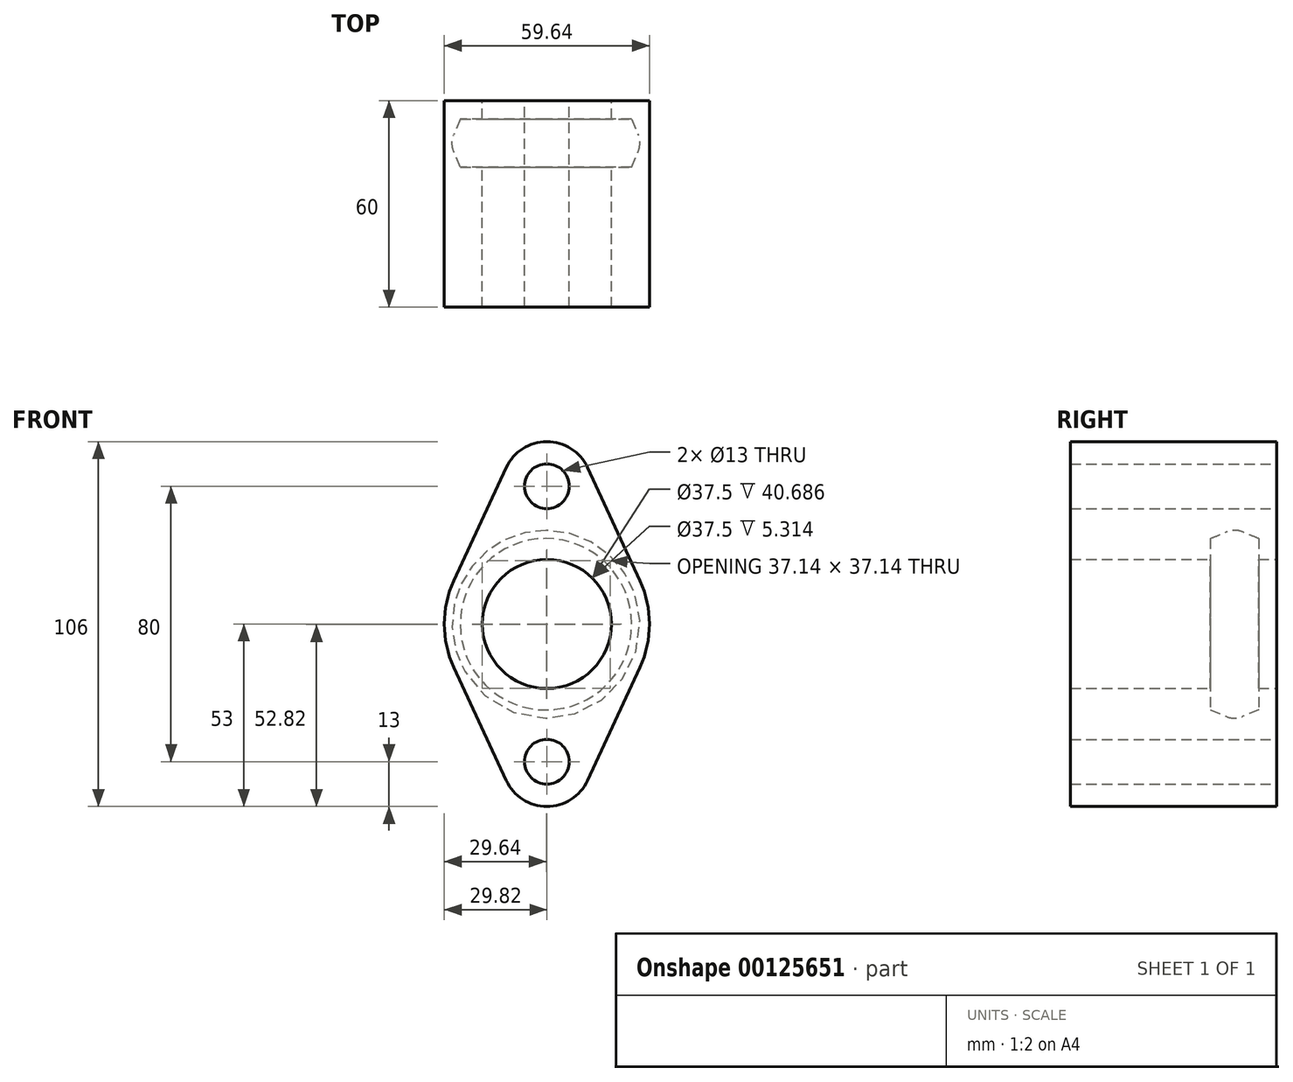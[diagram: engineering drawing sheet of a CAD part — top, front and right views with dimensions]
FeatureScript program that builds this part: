
annotation { "Feature Type Name" : "Feature", "Feature Type Description" : "" }
export const myFeature = defineFeature(function(context is Context, id is Id, definition is map)
    precondition{}
    {
        {
            var Q0;
            Q0=qCreatedBy(makeId("Front.planeOp"),FACE);
            var sketch = newSketch(context, id + "F0", { "sketchPlane" : qUnion([Q0])});
            skCircle(sketch, "E0", {"center": v(0, 0) * mm, "radius": 18.75 * mm});
            skCircle(sketch, "E1", {"center": v(0, 40) * mm, "radius": 6.5 * mm});
            skCircle(sketch, "E2", {"center": v(0, -40) * mm, "radius": 6.5 * mm});
            skArc(sketch, "E3", {"start": v(-27.05, 12.53) * mm, "mid": v(-29.82, 0) * mm, "end": v(-27.05, -12.53) * mm});
            skCircle(sketch, "E4", {"center": v(0, 0) * mm, "radius": 27.28 * mm, "construction": true});
            skLineSegment(sketch, "E5", {"start": v(0, 0) * mm, "end": v(14.78, 0) * mm});
            skCircle(sketch, "E6", {"center": v(21.03, 0) * mm, "radius": 6.25 * mm});
            skLineSegment(sketch, "E7", {"start": v(72.43, 27.8) * mm, "end": v(65.43, 24.9) * mm});
            skLineSegment(sketch, "E8.MirrorCS", {"start": v(72.43, 27.8) * mm, "end": v(79.43, 24.9) * mm});
            skArc(sketch, "E9", {"start": v(73.58, 27.32) * mm, "mid": v(72.43, 27.55) * mm, "end": v(71.29, 27.32) * mm});
            skCircle(sketch, "E10", {"center": v(72.43, 21.03) * mm, "radius": 6.25 * mm});
            skPoint(sketch, "E11", {"position": v(72.43, 27.28) * mm});
            skArc(sketch, "E12", {"start": v(11.8, 45.46) * mm, "mid": v(0, 53) * mm, "end": v(-11.8, 45.46) * mm});
            skArc(sketch, "E13", {"start": v(-11.8, -45.46) * mm, "mid": v(0, -53) * mm, "end": v(11.8, -45.46) * mm});
            skLineSegment(sketch, "E14", {"start": v(11.8, -45.46) * mm, "end": v(27.05, -12.53) * mm});
            skLineSegment(sketch, "E15", {"start": v(-27.05, -12.53) * mm, "end": v(-11.8, -45.46) * mm});
            skLineSegment(sketch, "E16.MirrorCS", {"start": v(11.8, 45.46) * mm, "end": v(27.05, 12.53) * mm});
            skLineSegment(sketch, "E17.MirrorCS", {"start": v(-27.05, 12.53) * mm, "end": v(-11.8, 45.46) * mm});
            skArc(sketch, "E18.trimOffspring", {"start": v(27.05, -12.53) * mm, "mid": v(29.82, 0) * mm, "end": v(27.05, 12.53) * mm});
            skLineSegment(sketch, "E19", {"start": v(65.43, 24.9) * mm, "end": v(65.43, 0) * mm});
            skLineSegment(sketch, "E20", {"start": v(79.43, 24.9) * mm, "end": v(79.43, 0) * mm});
            skLineSegment(sketch, "E21", {"start": v(65.43, 0) * mm, "end": v(79.43, 0) * mm});
            skLineSegment(sketch, "E22", {"start": v(72.43, 0) * mm, "end": v(72.43, 34.75) * mm, "construction": true});
            skPoint(sketch, "E23", {"position": v(72.43, 14.78) * mm});
            skPoint(sketch, "E24", {"position": v(72.43, 27.55) * mm});
            skSolve(sketch);
        }
        {
            var Q0;
            Q0=makeQuery(id+"F0.imprint","IMPRINT",FACE,{"disambiguationData":[TD([[makeQuery(id+"F0.imprint","IMPRINT",EDGE,{"derivedFrom":sQuery(id+"F0.wireOp",EDGE,"E2")}),-1.0]])]});
            var Q1;
            Q1=makeQuery(id+"F0.imprint","IMPRINT",FACE,{"disambiguationData":[TD([[makeQuery(id+"F0.imprint","IMPRINT",EDGE,{"derivedFrom":sQuery(id+"F0.wireOp",EDGE,"E1")}),-1.0]])]});
            var Q2;
            {var subQ4=sQuery(id+"F0.wireOp",EDGE,"E6");var subQ5=sQuery(id+"F0.wireOp",EDGE,"E0");var subQ6=makeQuery(id+"F0.imprint","INTERSECT",VERTEX,{"disambiguationData":[OD(0.0)],"derivedFrom":[subQ5,subQ4]});Q2=makeQuery(id+"F0.imprint","IMPRINT",FACE,{"disambiguationData":[TD([[makeQuery(id+"F0.imprint","IMPRINT",EDGE,{"disambiguationData":[TD([[subQ6,-1.0]])],"derivedFrom":subQ5}),-1.0]])]});}
            var Q3;
            {var subQ2=sQuery(id+"F0.wireOp",EDGE,"dtomJ7Fd-0WLo-ZkqJ-WQn9-IVpYXqV9S4C0");var subQ6=sQuery(id+"F0.wireOp",EDGE,"E0");var subQ7=makeQuery(id+"F0.imprint","INTERSECT",VERTEX,{"disambiguationData":[OD(1.0)],"derivedFrom":[subQ6,subQ2]});Q3=makeQuery(id+"F0.imprint","IMPRINT",FACE,{"disambiguationData":[TD([[makeQuery(id+"F0.imprint","IMPRINT",EDGE,{"disambiguationData":[TD([[subQ7,-1.0]])],"derivedFrom":subQ6}),-1.0]])]});}
            var Q4;
            Q4=sQuery(id+"F0.wireOp",EDGE,"E0");
            var Q5;
            Q5=sQuery(id+"F0.wireOp",EDGE,"E1");
            var Q6;
            Q6=sQuery(id+"F0.wireOp",EDGE,"E2");
            var Q7;
            Q7=sQuery(id+"F0.wireOp",EDGE,"E13");
            var Q8;
            Q8=sQuery(id+"F0.wireOp",EDGE,"E15");
            var Q9;
            Q9=sQuery(id+"F0.wireOp",EDGE,"E17.MirrorCS");
            var Q10;
            Q10=sQuery(id+"F0.wireOp",EDGE,"E12");
            var Q11;
            Q11=sQuery(id+"F0.wireOp",EDGE,"E16.MirrorCS");
            var Q12;
            Q12=sQuery(id+"F0.wireOp",EDGE,"E3");
            var Q13;
            Q13=sQuery(id+"F0.wireOp",EDGE,"E18.trimOffspring");
            var Q14;
            Q14=sQuery(id+"F0.wireOp",EDGE,"E14");
            extrude(context, id + "F1", {"entities" : qUnion([Q0, Q1, Q2, Q3]), "surfaceEntities" : qUnion([Q4, Q5, Q6, Q7, Q8, Q9, Q10, Q11, Q12, Q13, Q14]), "depth" : 60 * mm});
        }
        {
            var Q0;
            {var subQ6=sQuery(id+"F0.wireOp",EDGE,"E19");Q0=makeQuery(id+"F0.imprint","IMPRINT",FACE,{"disambiguationData":[TD([[makeQuery(id+"F0.imprint","IMPRINT",EDGE,{"derivedFrom":subQ6}),1.0]])]});}
            var Q1;
            {var subQ0=sQuery(id+"F0.wireOp",EDGE,"E10");var subQ1=makeQuery(id+"F0.imprint","INTERSECT",VERTEX,{"derivedFrom":[sQuery(id+"F0.wireOp",EDGE,"E7"),subQ0]});Q1=makeQuery(id+"F0.imprint","IMPRINT",FACE,{"disambiguationData":[TD([[makeQuery(id+"F0.imprint","IMPRINT",EDGE,{"disambiguationData":[TD([[subQ1,1.0]])],"derivedFrom":subQ0}),1.0]])]});}
            var Q2;
            Q2=sQuery(id+"F0.wireOp",EDGE,"E8.MirrorCS");
            var Q3;
            Q3=sQuery(id+"F0.wireOp",EDGE,"E7");
            var Q4;
            Q4=sQuery(id+"F0.wireOp",EDGE,"E21");
            revolve(context, id + "F2", {"entities" : qUnion([Q0, Q1]), "surfaceEntities" : qUnion([Q2, Q3]), "axis" : qUnion([Q4]), "revolveType" : RevolveType.FULL});
        }
        {
            var Q0;
            Q0=makeQuery(id+"F2.opRevolve","SWEPT_BODY",BODY,{"disambiguationData":[OSD([sQuery(id+"F0.wireOp",EDGE,"E7"),sQuery(id+"F0.wireOp",EDGE,"E8.MirrorCS"),sQuery(id+"F0.wireOp",EDGE,"E10"),sQuery(id+"F0.wireOp",EDGE,"E19"),sQuery(id+"F0.wireOp",EDGE,"E20"),sQuery(id+"F0.wireOp",EDGE,"E21")])]});
            var Q1;
            Q1=sQuery(id+"F0.wireOp",EDGE,"E22");
            transform(context, id + "F3", {"entities" : qUnion([Q0]), "transformType" : TransformType.ROTATION, "transformAxis" : qUnion([Q1]), "angle" : 90 * degree, "makeCopy" : false});
        }
        {
            var Q0;
            Q0=makeQuery(id+"F2.opRevolve","SWEPT_BODY",BODY,{"disambiguationData":[OSD([sQuery(id+"F0.wireOp",EDGE,"E7"),sQuery(id+"F0.wireOp",EDGE,"E8.MirrorCS"),sQuery(id+"F0.wireOp",EDGE,"E10"),sQuery(id+"F0.wireOp",EDGE,"E19"),sQuery(id+"F0.wireOp",EDGE,"E20"),sQuery(id+"F0.wireOp",EDGE,"E21")])]});
            transform(context, id + "F4", {"entities" : qUnion([Q0]), "transformType" : TransformType.TRANSLATION_3D, "dx" : -72.7 * mm, "dy" : -12.3 * mm, "dz" : -0.08 * mm, "makeCopy" : false});
        }
        {
            var Q0;
            Q0=makeQuery(id+"F2.opRevolve","SWEPT_BODY",BODY,{"disambiguationData":[OSD([sQuery(id+"F0.wireOp",EDGE,"E7"),sQuery(id+"F0.wireOp",EDGE,"E8.MirrorCS"),sQuery(id+"F0.wireOp",EDGE,"E10"),sQuery(id+"F0.wireOp",EDGE,"E19"),sQuery(id+"F0.wireOp",EDGE,"E20"),sQuery(id+"F0.wireOp",EDGE,"E21")])]});
            var Q1;
            Q1=makeQuery(id+"F1.opExtrude","SWEPT_BODY",BODY,{"disambiguationData":[OSD([sQuery(id+"F0.wireOp",EDGE,"E0"),sQuery(id+"F0.wireOp",EDGE,"E1"),sQuery(id+"F0.wireOp",EDGE,"E2"),sQuery(id+"F0.wireOp",EDGE,"E3"),sQuery(id+"F0.wireOp",EDGE,"E12"),sQuery(id+"F0.wireOp",EDGE,"E13"),sQuery(id+"F0.wireOp",EDGE,"E14"),sQuery(id+"F0.wireOp",EDGE,"E15"),sQuery(id+"F0.wireOp",EDGE,"E16.MirrorCS"),sQuery(id+"F0.wireOp",EDGE,"E17.MirrorCS"),sQuery(id+"F0.wireOp",EDGE,"E18.trimOffspring")])]});
            booleanBodies(context, id + "F5", {"operationType" : BooleanOperationType.SUBTRACTION, "tools" : qUnion([Q0]), "targets" : qUnion([Q1])});
        }
    });
